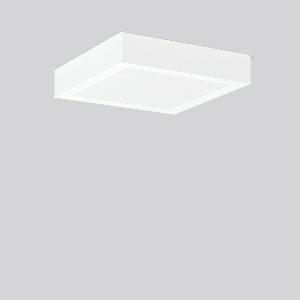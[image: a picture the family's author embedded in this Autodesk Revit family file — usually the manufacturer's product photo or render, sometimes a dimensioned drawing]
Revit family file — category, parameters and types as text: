
# Revit family: toledo_flat_square_a_672278_002_fb6a
name_source: partatom
category: Lighting Fixtures
units: mm (PartAtom-declared; Revit-internal decimal feet)

## family parameters
Cut with Voids When Loaded = No
Host = Face
Light Source = No
Part Type = Normal
Room Calculation Point = No
Round Connector Dimension = Use Diameter
Shared = No

## types (1)
- TOLEDO FLAT square A (1 x LED Modul 830, 2050 lm, 3000)
    Apparent Load = 25 VA
    CIE Flux Codes = 48 80 96 100 100
    Color Rendering = 80
    Color Temperature = 3000
    Default Elevation = 1800 mm
    Description = Series: TOLEDO FLAT square
Ultra thin surface mounted downlight. For escape route illumination. Surface mounted housing: sheet steel, powder-coated. Square cover plate: die-cast aluminium, powder coated. Light guide and diffuser made of non-yellowing PMMA, opal matt. Betriebsgeräte integriert. Einzelbatteriesystem mit automatischem Selbsttest. 
Colour: white
Length: 300 mm
Width: 300 mm
Height: 58 mm
Weight: 3.95 kg
Operating mode: maintained power mode
Duration time: 8 h
Lamp: LED
Socket: without socket
Colour temperature: 3000K
Colour rendering index (CRI): 80
System power: 25 W
Rated luminous flux: 2050 lm
Luminous flux, emergency: 170 lm
System power, emergency: -
Control gear: Regulated power supply
Protection class: I
Type of protection: IP 40
    Height = 58 mm
    Lamp = 1 x LED Modul 830
    Lamp Light Flux = 2050 lm
    Lamp count = 1
    Length = 300 mm
    Lifetime = 50000 h
    Luminous efficacy = 82 lm/W
    Manufacturer = RZB
    ModVariant = No
    Model = 672278.002
    Mounting Place = Ceiling
    Mounting Type = Surface mounted
    Number of Poles = 1
    OnlyDefault = Yes
    Power Factor = 1
    Product Name = TOLEDO FLAT square A
    Product group = Surface mounted downlights
    ProductGroupID = 302
    Protection Class = Protection class I
    Protection Degree = IP 40
    RLX_Detail_Level = 1
    RLX_Emergency_Light_Flux = 170 lm
    RLX_Emergency_Type = 3
    RLX_Emergency_Type_DB = Yes
    RlxData = <blob elided: 13933 chars, md5=8eb72bc3>
    Socket = socket
    Standby Power = 0 W
    System Light Flux = 2050 lm
    System Power = 25 W
    Type Comments = Product without accessories
    Type Image = 901554.002.jpg
    URL = http://relux.com
    VarID = ---
    Voltage = 0 V
    Weight = 0.00 kg
    Width = 300 mm

## geometry (parser evidence)
native form markers: Sweep x13
no freeform markers — native parametric forms only
